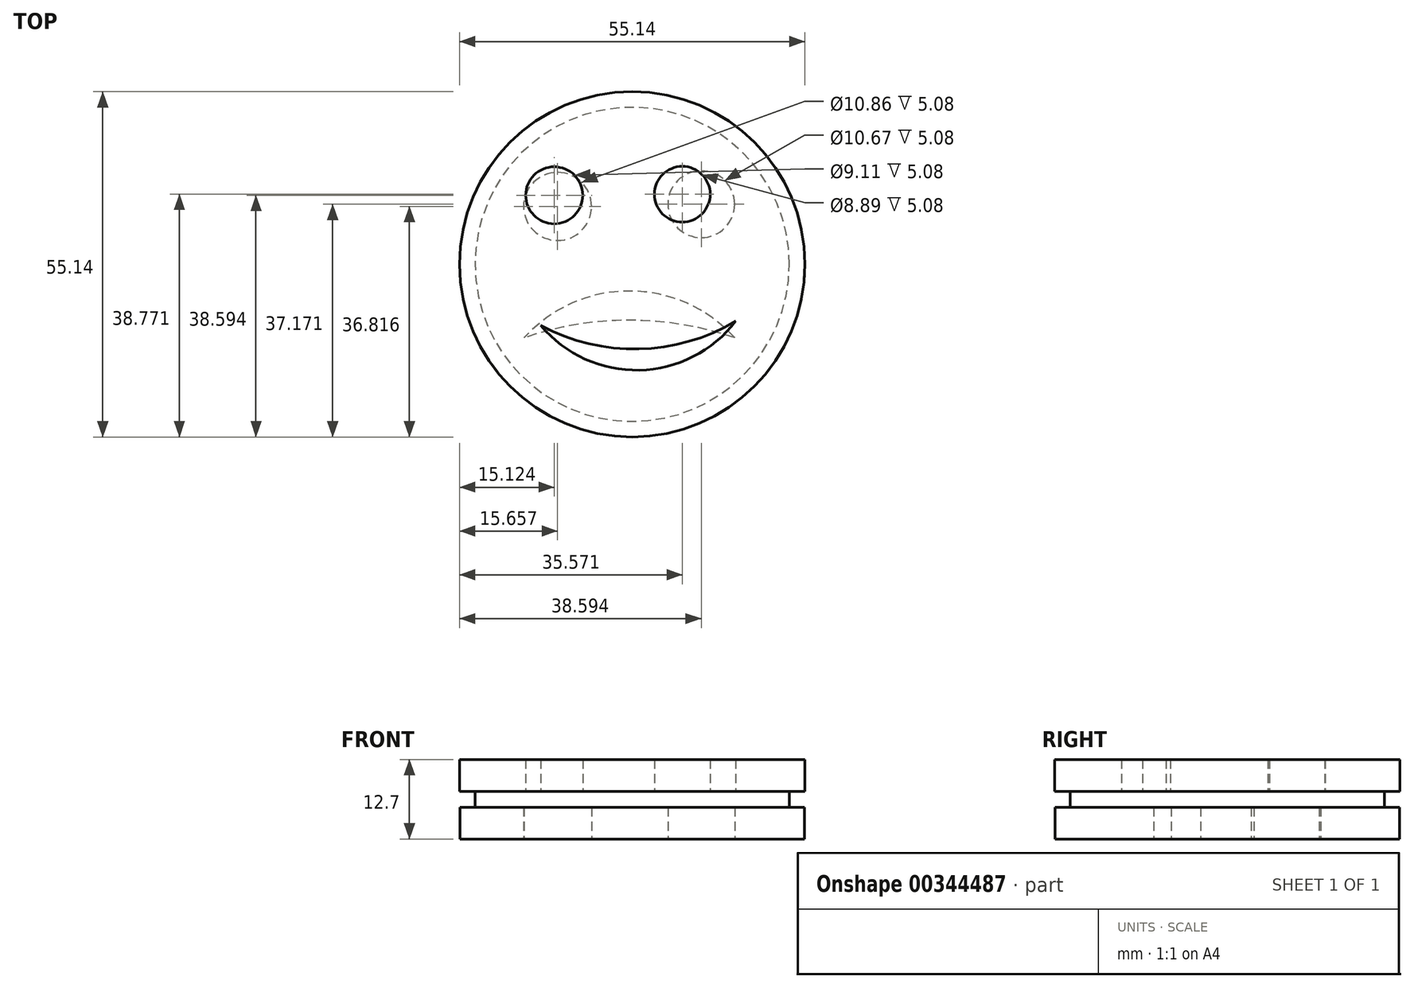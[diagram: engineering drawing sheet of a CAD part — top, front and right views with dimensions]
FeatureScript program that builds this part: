
annotation { "Feature Type Name" : "Feature", "Feature Type Description" : "" }
export const myFeature = defineFeature(function(context is Context, id is Id, definition is map)
    precondition{}
    {
        {
            var Q0;
            Q0=qCreatedBy(makeId("Top.planeOp"),FACE);
            var sketch = newSketch(context, id + "F0", { "sketchPlane" : qUnion([Q0])});
            skCircle(sketch, "E0", {"center": v(0, 0) * mm, "radius": 27.51 * mm});
            skCircle(sketch, "E1", {"center": v(-11.91, 9.25) * mm, "radius": 5.43 * mm});
            skCircle(sketch, "E2", {"center": v(11.02, 9.6) * mm, "radius": 5.34 * mm});
            skArc(sketch, "E3", {"start": v(16.36, -11.73) * mm, "mid": v(-0.44, -4.27) * mm, "end": v(-17.25, -11.73) * mm});
            skArc(sketch, "E4", {"start": v(16.36, -11.73) * mm, "mid": v(-0.44, -8.93) * mm, "end": v(-17.25, -11.73) * mm});
            skSolve(sketch);
        }
        {
            var Q0;
            Q0=makeQuery(id+"F0.imprint","IMPRINT",FACE,{"disambiguationData":[TD([[makeQuery(id+"F0.imprint","IMPRINT",EDGE,{"derivedFrom":sQuery(id+"F0.wireOp",EDGE,"E0")}),1.0]])]});
            extrude(context, id + "F1", {"entities" : qUnion([Q0]), "depth" : 5.08 * mm});
        }
        {
            var Q0;
            Q0=makeQuery(id+"F1.opExtrude","CAP_FACE",FACE,{"disambiguationData":[OSD([sQuery(id+"F0.wireOp",EDGE,"E0"),sQuery(id+"F0.wireOp",EDGE,"E1"),sQuery(id+"F0.wireOp",EDGE,"E2"),sQuery(id+"F0.wireOp",EDGE,"E3"),sQuery(id+"F0.wireOp",EDGE,"E4")])],"isStart":false});
            var sketch = newSketch(context, id + "F2", { "sketchPlane" : qUnion([Q0])});
            skCircle(sketch, "E5", {"center": v(0, 0) * mm, "radius": 25.08 * mm});
            skSolve(sketch);
        }
        {
            var Q0;
            Q0 = qSketchRegion(id + "F2", true);
            extrude(context, id + "F3", {"entities" : qUnion([Q0]), "operationType" : NewBodyOperationType.ADD, "depth" : 2.54 * mm});
        }
        {
            var Q0;
            Q0=makeQuery(id+"F3.opExtrude","CAP_FACE",FACE,{"disambiguationData":[OSD([sQuery(id+"F2.wireOp",EDGE,"E5")])],"isStart":false});
            var sketch = newSketch(context, id + "F4", { "sketchPlane" : qUnion([Q0])});
            skCircle(sketch, "E6", {"center": v(0, 0) * mm, "radius": 27.57 * mm});
            skCircle(sketch, "E7", {"center": v(-12.45, 11.02) * mm, "radius": 4.55 * mm});
            skCircle(sketch, "E8", {"center": v(8, 11.2) * mm, "radius": 4.44 * mm});
            skArc(sketch, "E9", {"start": v(-14.58, -9.78) * mm, "mid": v(1.15, -16.9) * mm, "end": v(16.54, -9.07) * mm});
            skArc(sketch, "E10", {"start": v(-14.58, -9.78) * mm, "mid": v(1.07, -13.52) * mm, "end": v(16.54, -9.07) * mm});
            skSolve(sketch);
        }
        {
            var Q0;
            Q0 = qSketchRegion(id + "F4", true);
            extrude(context, id + "F5", {"entities" : qUnion([Q0]), "operationType" : NewBodyOperationType.ADD, "depth" : 5.08 * mm});
        }
    });
